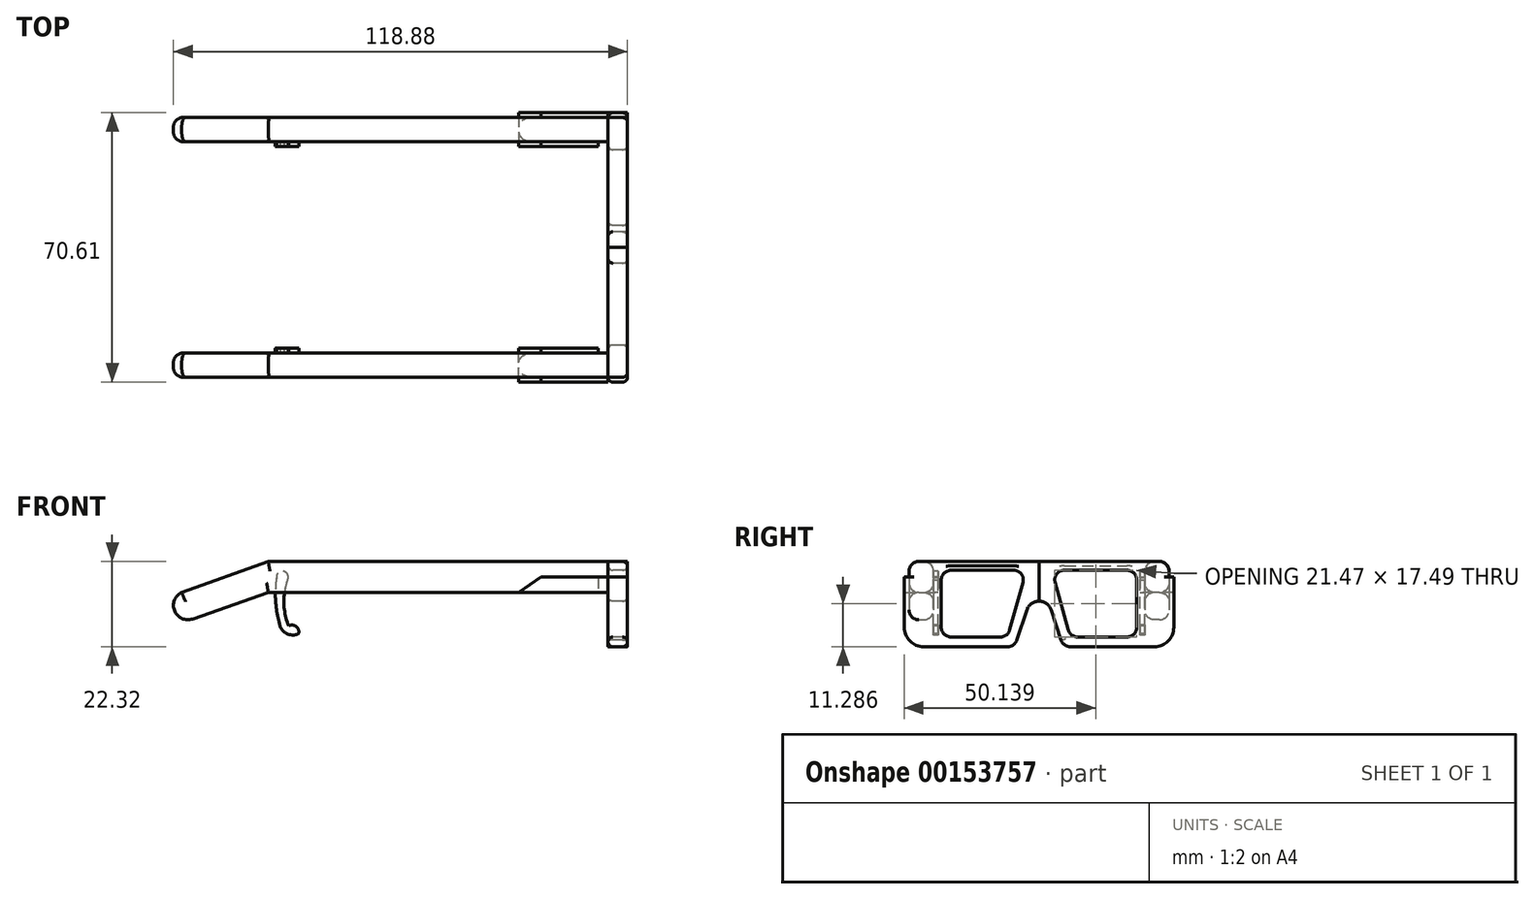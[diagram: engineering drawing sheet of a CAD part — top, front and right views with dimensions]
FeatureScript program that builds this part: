
annotation { "Feature Type Name" : "Feature", "Feature Type Description" : "" }
export const myFeature = defineFeature(function(context is Context, id is Id, definition is map)
    precondition{}
    {
        {
            var Q0;
            Q0=qCreatedBy(makeId("Front.planeOp"),FACE);
            var sketch = newSketch(context, id + "F0", { "sketchPlane" : qUnion([Q0])});
            skLineSegment(sketch, "E0", {"start": v(0, 0) * mm, "end": v(-86.43, 0) * mm});
            skLineSegment(sketch, "E1", {"start": v(0, 0) * mm, "end": v(0, -8.13) * mm});
            skLineSegment(sketch, "E2", {"start": v(0, -8.13) * mm, "end": v(-86.43, -8.13) * mm});
            skLineSegment(sketch, "E3", {"start": v(0, -4.06) * mm, "end": v(-15.06, -4.06) * mm});
            skLineSegment(sketch, "E4", {"start": v(-15.06, -4.06) * mm, "end": v(-20.83, -8.13) * mm});
            skLineSegment(sketch, "E5", {"start": v(-86.43, -8.13) * mm, "end": v(-106.28, -15.05) * mm});
            skArc(sketch, "E6", {"start": v(-106.28, -15.05) * mm, "mid": v(-110.98, -12.93) * mm, "end": v(-109.1, -8.13) * mm});
            skLineSegment(sketch, "E7", {"start": v(-86.43, 0) * mm, "end": v(-109.1, -8.13) * mm});
            skSolve(sketch);
        }
        {
            var Q0;
            {var subQ5=sQuery(id+"F0.wireOp",EDGE,"E0");Q0=makeQuery(id+"F0.imprint","IMPRINT",FACE,{"disambiguationData":[TD([[makeQuery(id+"F0.imprint","IMPRINT",EDGE,{"derivedFrom":subQ5}),1.0]])]});}
            extrude(context, id + "F1", {"entities" : qUnion([Q0]), "depth" : 6.35 * mm});
        }
        {
            var Q0;
            {var subQ3=sQuery(id+"F0.wireOp",EDGE,"E3");Q0=makeQuery(id+"F0.imprint","IMPRINT",FACE,{"disambiguationData":[TD([[makeQuery(id+"F0.imprint","IMPRINT",EDGE,{"derivedFrom":subQ3}),1.0]])]});}
            extrude(context, id + "F2", {"entities" : qUnion([Q0]), "depth" : 7.62 * mm});
        }
        {
            var Q0;
            Q0=makeQuery(id+"F1.opExtrude","CAP_EDGE",EDGE,{"disambiguationData":[OSD([sQuery(id+"F0.wireOp",EDGE,"E0")])],"isStart":false});
            var Q1;
            Q1=makeQuery(id+"F1.opExtrude","CAP_EDGE",EDGE,{"disambiguationData":[OSD([sQuery(id+"F0.wireOp",EDGE,"E0")])],"isStart":true});
            var Q2;
            Q2=makeQuery(id+"F1.opExtrude","CAP_EDGE",EDGE,{"disambiguationData":[OSD([sQuery(id+"F0.wireOp",EDGE,"E7")])],"isStart":false});
            var Q3;
            Q3=makeQuery(id+"F1.opExtrude","CAP_EDGE",EDGE,{"disambiguationData":[OSD([sQuery(id+"F0.wireOp",EDGE,"E7")])],"isStart":true});
            var Q4;
            Q4=makeQuery(id+"F1.opExtrude","CAP_EDGE",EDGE,{"disambiguationData":[OSD([sQuery(id+"F0.wireOp",EDGE,"E2")])],"isStart":false});
            var Q5;
            Q5=makeQuery(id+"F1.opExtrude","CAP_EDGE",EDGE,{"disambiguationData":[OSD([sQuery(id+"F0.wireOp",EDGE,"E5")])],"isStart":false});
            var Q6;
            Q6=makeQuery(id+"F1.opExtrude","CAP_EDGE",EDGE,{"disambiguationData":[OSD([sQuery(id+"F0.wireOp",EDGE,"E2")])],"isStart":true});
            var Q7;
            Q7=makeQuery(id+"F1.opExtrude","CAP_EDGE",EDGE,{"disambiguationData":[OSD([sQuery(id+"F0.wireOp",EDGE,"E5")])],"isStart":true});
            fillet(context, id + "F3", {"entities" : qUnion([Q0, Q1, Q2, Q3, Q4, Q5, Q6, Q7]), "radius" : 2.54 * mm, "tangentPropagation" : true, "allowEdgeOverflow" : false});
        }
        {
            var Q0;
            Q0=makeQuery(id+"F1.opExtrude","SWEPT_FACE",FACE,{"disambiguationData":[OSD([sQuery(id+"F0.wireOp",EDGE,"E1")])]});
            var Q1;
            Q1=makeQuery(id+"F2.opExtrude","SWEPT_FACE",FACE,{"disambiguationData":[OSD([sQuery(id+"F0.wireOp",EDGE,"E1")])]});
            extrude(context, id + "F4", {"entities" : qUnion([Q0, Q1]), "operationType" : NewBodyOperationType.ADD, "depth" : 2.54 * mm});
        }
        {
            var Q0;
            {var subQ3=sQuery(id+"F0.wireOp",EDGE,"E3");Q0=makeQuery(id+"F0.imprint","IMPRINT",FACE,{"disambiguationData":[TD([[makeQuery(id+"F0.imprint","IMPRINT",EDGE,{"derivedFrom":subQ3}),1.0]])]});}
            extrude(context, id + "F5", {"entities" : qUnion([Q0]), "operationType" : NewBodyOperationType.ADD, "oppositeDirection" : true, "depth" : 1.27 * mm});
        }
        {
            var Q0;
            {var subQ0=sQuery(id+"F0.wireOp",EDGE,"E1");Q0=makeQuery(id+"F4.boolean.opBoolean","MERGE",FACE,{"derivedFrom":[makeQuery(id+"F4.opExtrude","CAP_FACE",FACE,{"disambiguationData":[OSD([subQ0]),TDD([makeQuery(id+"F2.opExtrude","SWEPT_FACE",FACE,{"disambiguationData":[OSD([subQ0])]})])],"isStart":false}),makeQuery(id+"F4.opExtrude","CAP_FACE",FACE,{"disambiguationData":[OSD([subQ0]),TDD([makeQuery(id+"F1.opExtrude","SWEPT_FACE",FACE,{"disambiguationData":[OSD([subQ0])]})])],"isStart":false})]});}
            var sketch = newSketch(context, id + "F6", { "sketchPlane" : qUnion([Q0])});
            skLineSegment(sketch, "E8", {"start": v(-7.62, -8.13) * mm, "end": v(-7.62, -4.06) * mm});
            skLineSegment(sketch, "E9", {"start": v(-7.62, -4.06) * mm, "end": v(-6.35, -4.06) * mm});
            skLineSegment(sketch, "E10", {"start": v(-7.62, -8.13) * mm, "end": v(-7.62, -17.24) * mm});
            skLineSegment(sketch, "E11", {"start": v(-2.54, -22.32) * mm, "end": v(19.47, -22.32) * mm});
            skLineSegment(sketch, "E12", {"start": v(-3.81, 0) * mm, "end": v(-2.54, 0) * mm});
            skLineSegment(sketch, "E13", {"start": v(-6.35, -4.06) * mm, "end": v(-6.35, -2.54) * mm});
            skArc(sketch, "E14", {"start": v(-3.81, 0) * mm, "mid": v(-5.6, -0.74) * mm, "end": v(-6.35, -2.54) * mm});
            skPoint(sketch, "E15.visualSharp", {"position": v(-7.62, -22.32) * mm});
            skArc(sketch, "E15.filletArc", {"start": v(-7.62, -17.24) * mm, "mid": v(-6.13, -20.83) * mm, "end": v(-2.54, -22.32) * mm});
            skLineSegment(sketch, "E16", {"start": v(21.89, -20.58) * mm, "end": v(24.49, -12.69) * mm});
            skLineSegment(sketch, "E17", {"start": v(34.02, -22.32) * mm, "end": v(30.84, -12.69) * mm});
            skArc(sketch, "E18", {"start": v(30.84, -12.69) * mm, "mid": v(27.66, -10.39) * mm, "end": v(24.49, -12.69) * mm});
            skPoint(sketch, "E19.visualSharp", {"position": v(21.31, -22.32) * mm});
            skArc(sketch, "E19.filletArc", {"start": v(19.47, -22.32) * mm, "mid": v(20.96, -21.84) * mm, "end": v(21.89, -20.58) * mm});
            skLineSegment(sketch, "E20", {"start": v(-2.54, 0) * mm, "end": v(27.66, 0) * mm});
            skPoint(sketch, "E20.endSnap0", {"position": v(27.66, -10.39) * mm});
            skLineSegment(sketch, "E21", {"start": v(27.66, 0) * mm, "end": v(27.66, -10.39) * mm});
            skArc(sketch, "E22.MirrorCS", {"start": v(59.14, 0) * mm, "mid": v(60.93, -0.74) * mm, "end": v(61.68, -2.54) * mm});
            skLineSegment(sketch, "E23.MirrorCS", {"start": v(61.68, -4.06) * mm, "end": v(61.68, -2.54) * mm});
            skLineSegment(sketch, "E24.MirrorCS", {"start": v(62.95, -4.06) * mm, "end": v(61.68, -4.06) * mm});
            skLineSegment(sketch, "E25.MirrorCS", {"start": v(62.95, -8.13) * mm, "end": v(62.95, -4.06) * mm});
            skLineSegment(sketch, "E26.MirrorCS", {"start": v(62.95, -8.13) * mm, "end": v(62.95, -17.24) * mm});
            skArc(sketch, "E27.MirrorCS", {"start": v(62.95, -17.24) * mm, "mid": v(61.46, -20.83) * mm, "end": v(57.87, -22.32) * mm});
            skLineSegment(sketch, "E28.MirrorCS", {"start": v(57.87, -22.32) * mm, "end": v(35.85, -22.32) * mm});
            skLineSegment(sketch, "E29.MirrorCS", {"start": v(57.87, 0) * mm, "end": v(27.66, 0) * mm});
            skLineSegment(sketch, "E30.MirrorCS", {"start": v(59.14, 0) * mm, "end": v(57.87, 0) * mm});
            skArc(sketch, "E31.MirrorCS", {"start": v(35.85, -22.32) * mm, "mid": v(34.37, -21.84) * mm, "end": v(33.44, -20.58) * mm});
            skLineSegment(sketch, "E32", {"start": v(23.45, -5.51) * mm, "end": v(20, -17.92) * mm});
            skLineSegment(sketch, "E33", {"start": v(21, -2.29) * mm, "end": v(4.61, -2.29) * mm});
            skLineSegment(sketch, "E34", {"start": v(2.07, -4.83) * mm, "end": v(2.07, -17.24) * mm});
            skLineSegment(sketch, "E35", {"start": v(4.61, -19.78) * mm, "end": v(17.55, -19.78) * mm});
            skPoint(sketch, "E36.visualSharp", {"position": v(2.07, -19.78) * mm});
            skArc(sketch, "E36.filletArc", {"start": v(2.07, -17.24) * mm, "mid": v(2.82, -19.04) * mm, "end": v(4.61, -19.78) * mm});
            skPoint(sketch, "E37.visualSharp", {"position": v(24.35, -2.29) * mm});
            skArc(sketch, "E37.filletArc", {"start": v(23.45, -5.51) * mm, "mid": v(23.03, -3.3) * mm, "end": v(21, -2.29) * mm});
            skPoint(sketch, "E38.visualSharp", {"position": v(2.07, -2.29) * mm});
            skArc(sketch, "E38.filletArc", {"start": v(4.61, -2.29) * mm, "mid": v(2.82, -3.03) * mm, "end": v(2.07, -4.83) * mm});
            skArc(sketch, "E39.filletArc", {"start": v(17.55, -19.78) * mm, "mid": v(19.08, -19.26) * mm, "end": v(20, -17.92) * mm});
            skArc(sketch, "E40.MirrorCS", {"start": v(31.87, -5.51) * mm, "mid": v(32.3, -3.3) * mm, "end": v(34.32, -2.29) * mm});
            skLineSegment(sketch, "E41.MirrorCS", {"start": v(34.32, -2.29) * mm, "end": v(50.72, -2.29) * mm});
            skArc(sketch, "E42.MirrorCS", {"start": v(50.72, -2.29) * mm, "mid": v(52.51, -3.03) * mm, "end": v(53.26, -4.83) * mm});
            skLineSegment(sketch, "E43.MirrorCS", {"start": v(53.26, -4.83) * mm, "end": v(53.26, -17.24) * mm});
            skArc(sketch, "E44.MirrorCS", {"start": v(53.26, -17.24) * mm, "mid": v(52.51, -19.04) * mm, "end": v(50.72, -19.78) * mm});
            skLineSegment(sketch, "E45.MirrorCS", {"start": v(50.72, -19.78) * mm, "end": v(37.78, -19.78) * mm});
            skArc(sketch, "E46.MirrorCS", {"start": v(37.78, -19.78) * mm, "mid": v(36.25, -19.26) * mm, "end": v(35.34, -17.92) * mm});
            skLineSegment(sketch, "E47.MirrorCS", {"start": v(31.87, -5.51) * mm, "end": v(35.34, -17.92) * mm});
            skLineSegment(sketch, "E48", {"start": v(27.66, 0) * mm, "end": v(27.66, 9.6) * mm});
            skLineSegment(sketch, "E49", {"start": v(27.66, 9.6) * mm, "end": v(24.35, 0) * mm});
            skSolve(sketch);
        }
        {
            var Q0;
            Q0=makeQuery(id+"F6.imprint","IMPRINT",FACE,{"disambiguationData":[TD([[makeQuery(id+"F6.imprint","IMPRINT",EDGE,{"derivedFrom":sQuery(id+"F6.wireOp",EDGE,"E10")}),1.0]])]});
            var Q1;
            {var subQ0=sQuery(id+"F6.wireOp",EDGE,"E21");Q1=makeQuery(id+"F6.imprint","IMPRINT",FACE,{"disambiguationData":[TD([[makeQuery(id+"F6.imprint","IMPRINT",EDGE,{"derivedFrom":subQ0}),1.0]])]});}
            var Q2;
            Q2=makeQuery(id+"F6.imprint","IMPRINT",FACE,{"disambiguationData":[TD([[makeQuery(id+"F6.imprint","IMPRINT",EDGE,{"derivedFrom":sQuery(id+"F6.wireOp",EDGE,"E8")}),1.0]])]});
            extrude(context, id + "F7", {"entities" : qUnion([Q0, Q1, Q2]), "depth" : 5.08 * mm});
        }
        {
            var Q0;
            Q0=makeQuery(id+"F6.imprint","IMPRINT",FACE,{"disambiguationData":[TD([[makeQuery(id+"F6.imprint","IMPRINT",EDGE,{"derivedFrom":sQuery(id+"F6.wireOp",EDGE,"E32")}),-1.0]])]});
            var Q1;
            Q1=makeQuery(id+"F6.imprint","IMPRINT",FACE,{"disambiguationData":[TD([[makeQuery(id+"F6.imprint","IMPRINT",EDGE,{"derivedFrom":sQuery(id+"F6.wireOp",EDGE,"E40.MirrorCS")}),-1.0]])]});
            var Q2;
            Q2=makeQuery(id+"F7.opExtrude","CAP_FACE",FACE,{"disambiguationData":[OSD([sQuery(id+"F6.wireOp",EDGE,"E8"),sQuery(id+"F6.wireOp",EDGE,"E9"),sQuery(id+"F6.wireOp",EDGE,"E10"),sQuery(id+"F6.wireOp",EDGE,"E11"),sQuery(id+"F6.wireOp",EDGE,"E12"),sQuery(id+"F6.wireOp",EDGE,"E13"),sQuery(id+"F6.wireOp",EDGE,"E14"),sQuery(id+"F6.wireOp",EDGE,"E15.filletArc"),sQuery(id+"F6.wireOp",EDGE,"E16"),sQuery(id+"F6.wireOp",EDGE,"E17"),sQuery(id+"F6.wireOp",EDGE,"E18"),sQuery(id+"F6.wireOp",EDGE,"E19.filletArc"),sQuery(id+"F6.wireOp",EDGE,"E20"),sQuery(id+"F6.wireOp",EDGE,"E22.MirrorCS"),sQuery(id+"F6.wireOp",EDGE,"E23.MirrorCS"),sQuery(id+"F6.wireOp",EDGE,"E24.MirrorCS"),sQuery(id+"F6.wireOp",EDGE,"E25.MirrorCS"),sQuery(id+"F6.wireOp",EDGE,"E26.MirrorCS"),sQuery(id+"F6.wireOp",EDGE,"E27.MirrorCS"),sQuery(id+"F6.wireOp",EDGE,"E28.MirrorCS"),sQuery(id+"F6.wireOp",EDGE,"E29.MirrorCS"),sQuery(id+"F6.wireOp",EDGE,"E30.MirrorCS"),sQuery(id+"F6.wireOp",EDGE,"E31.MirrorCS"),sQuery(id+"F6.wireOp",EDGE,"E32"),sQuery(id+"F6.wireOp",EDGE,"E33"),sQuery(id+"F6.wireOp",EDGE,"E34"),sQuery(id+"F6.wireOp",EDGE,"E35"),sQuery(id+"F6.wireOp",EDGE,"E36.filletArc"),sQuery(id+"F6.wireOp",EDGE,"E37.filletArc"),sQuery(id+"F6.wireOp",EDGE,"E38.filletArc"),sQuery(id+"F6.wireOp",EDGE,"E39.filletArc"),sQuery(id+"F6.wireOp",EDGE,"E40.MirrorCS"),sQuery(id+"F6.wireOp",EDGE,"E41.MirrorCS"),sQuery(id+"F6.wireOp",EDGE,"E42.MirrorCS"),sQuery(id+"F6.wireOp",EDGE,"E43.MirrorCS"),sQuery(id+"F6.wireOp",EDGE,"E44.MirrorCS"),sQuery(id+"F6.wireOp",EDGE,"E45.MirrorCS"),sQuery(id+"F6.wireOp",EDGE,"E46.MirrorCS"),sQuery(id+"F6.wireOp",EDGE,"E47.MirrorCS")])],"isStart":false});
            extrude(context, id + "F8", {"entities" : qUnion([Q0, Q1]), "endBound" : BoundingType.UP_TO_SURFACE, "endBoundEntityFace" : qUnion([Q2]), "depth" : 25.4 * mm});
        }
        {
            var Q0;
            Q0=makeQuery(id+"F7.opExtrude","CAP_EDGE",EDGE,{"disambiguationData":[OSD([sQuery(id+"F6.wireOp",EDGE,"E12"),sQuery(id+"F6.wireOp",EDGE,"E20"),sQuery(id+"F6.wireOp",EDGE,"E29.MirrorCS"),sQuery(id+"F6.wireOp",EDGE,"E30.MirrorCS")])],"isStart":false});
            var Q1;
            Q1=makeQuery(id+"F7.opExtrude","CAP_EDGE",EDGE,{"disambiguationData":[OSD([sQuery(id+"F6.wireOp",EDGE,"E11")])],"isStart":false});
            var Q2;
            Q2=makeQuery(id+"F7.opExtrude","CAP_EDGE",EDGE,{"disambiguationData":[OSD([sQuery(id+"F6.wireOp",EDGE,"E28.MirrorCS")])],"isStart":false});
            var Q3;
            Q3=makeQuery(id+"F7.opExtrude","CAP_EDGE",EDGE,{"disambiguationData":[OSD([sQuery(id+"F6.wireOp",EDGE,"E41.MirrorCS")])],"isStart":false});
            var Q4;
            Q4=makeQuery(id+"F7.opExtrude","CAP_EDGE",EDGE,{"disambiguationData":[OSD([sQuery(id+"F6.wireOp",EDGE,"E43.MirrorCS")])],"isStart":true});
            var Q5;
            Q5=makeQuery(id+"F7.opExtrude","CAP_EDGE",EDGE,{"disambiguationData":[OSD([sQuery(id+"F6.wireOp",EDGE,"E33")])],"isStart":true});
            var Q6;
            Q6=makeQuery(id+"F7.opExtrude","CAP_EDGE",EDGE,{"disambiguationData":[OSD([sQuery(id+"F6.wireOp",EDGE,"E25.MirrorCS"),sQuery(id+"F6.wireOp",EDGE,"E26.MirrorCS")])],"isStart":true});
            var Q7;
            Q7=makeQuery(id+"F7.opExtrude","CAP_EDGE",EDGE,{"disambiguationData":[OSD([sQuery(id+"F6.wireOp",EDGE,"E28.MirrorCS")])],"isStart":true});
            var Q8;
            Q8=makeQuery(id+"F7.opExtrude","CAP_EDGE",EDGE,{"disambiguationData":[OSD([sQuery(id+"F6.wireOp",EDGE,"E11")])],"isStart":true});
            var Q9;
            Q9=makeQuery(id+"F7.opExtrude","CAP_EDGE",EDGE,{"disambiguationData":[OSD([sQuery(id+"F6.wireOp",EDGE,"E33")])],"isStart":false});
            fillet(context, id + "F9", {"entities" : qUnion([Q0, Q1, Q2, Q3, Q4, Q5, Q6, Q7, Q8, Q9]), "radius" : 1.27 * mm, "tangentPropagation" : true, "allowEdgeOverflow" : false});
        }
        {
            var Q0;
            Q0=makeQuery(id+"F1.opExtrude","SWEPT_BODY",BODY,{"disambiguationData":[OSD([sQuery(id+"F0.wireOp",EDGE,"E0"),sQuery(id+"F0.wireOp",EDGE,"E1"),sQuery(id+"F0.wireOp",EDGE,"E2"),sQuery(id+"F0.wireOp",EDGE,"E3"),sQuery(id+"F0.wireOp",EDGE,"E4"),sQuery(id+"F0.wireOp",EDGE,"E5"),sQuery(id+"F0.wireOp",EDGE,"E6"),sQuery(id+"F0.wireOp",EDGE,"E7")])]});
            var Q1;
            Q1=makeQuery(id+"F2.opExtrude","SWEPT_BODY",BODY,{"disambiguationData":[OSD([sQuery(id+"F0.wireOp",EDGE,"E1"),sQuery(id+"F0.wireOp",EDGE,"E2"),sQuery(id+"F0.wireOp",EDGE,"E3"),sQuery(id+"F0.wireOp",EDGE,"E4")])]});
            var Q2;
            Q2=qCreatedBy(makeId("Front.planeOp"),FACE);
            mirror(context, id + "F10", {"entities" : qUnion([Q0, Q1]), "mirrorPlane" : qUnion([Q2])});
        }
        {
            var Q0;
            Q0=makeQuery(id+"F10.opPattern","COPY",BODY,{"derivedFrom":makeQuery(id+"F2.opExtrude","SWEPT_BODY",BODY,{"disambiguationData":[OSD([sQuery(id+"F0.wireOp",EDGE,"E1"),sQuery(id+"F0.wireOp",EDGE,"E2"),sQuery(id+"F0.wireOp",EDGE,"E3"),sQuery(id+"F0.wireOp",EDGE,"E4")])]}),"instanceName":"1"});
            var Q1;
            Q1=makeQuery(id+"F10.opPattern","COPY",BODY,{"derivedFrom":makeQuery(id+"F1.opExtrude","SWEPT_BODY",BODY,{"disambiguationData":[OSD([sQuery(id+"F0.wireOp",EDGE,"E0"),sQuery(id+"F0.wireOp",EDGE,"E1"),sQuery(id+"F0.wireOp",EDGE,"E2"),sQuery(id+"F0.wireOp",EDGE,"E3"),sQuery(id+"F0.wireOp",EDGE,"E4"),sQuery(id+"F0.wireOp",EDGE,"E5"),sQuery(id+"F0.wireOp",EDGE,"E6"),sQuery(id+"F0.wireOp",EDGE,"E7")])]}),"instanceName":"1"});
            var Q2;
            {var subQ0=sQuery(id+"F6.wireOp",EDGE,"E30.MirrorCS");var subQ1=sQuery(id+"F6.wireOp",EDGE,"E29.MirrorCS");var subQ2=sQuery(id+"F6.wireOp",EDGE,"E20");var subQ3=sQuery(id+"F6.wireOp",EDGE,"E12");Q2=makeQuery(id+"F9.opFillet","BLEND_EDGE",EDGE,{"blendedFrom":[makeQuery(id+"F7.opExtrude","CAP_EDGE",EDGE,{"disambiguationData":[OSD([subQ3,subQ2,subQ1,subQ0])],"isStart":false}),makeQuery(id+"F7.opExtrude","SWEPT_FACE",FACE,{"disambiguationData":[OSD([subQ3,subQ2,subQ1,subQ0])]})],"blendedInto":[makeQuery(id+"F7.opExtrude","SWEPT_FACE",FACE,{"disambiguationData":[OSD([subQ3,subQ2,subQ1,subQ0])]})]});}
            transform(context, id + "F11", {"entities" : qUnion([Q0, Q1]), "transformType" : TransformType.TRANSLATION_DISTANCE, "transformDirection" : qUnion([Q2]), "distance" : 55.37 * mm, "makeCopy" : false});
        }
        {
            var Q0;
            Q0=makeQuery(id+"F1.opExtrude","CAP_FACE",FACE,{"disambiguationData":[OSD([sQuery(id+"F0.wireOp",EDGE,"E0"),sQuery(id+"F0.wireOp",EDGE,"E1"),sQuery(id+"F0.wireOp",EDGE,"E2"),sQuery(id+"F0.wireOp",EDGE,"E3"),sQuery(id+"F0.wireOp",EDGE,"E4"),sQuery(id+"F0.wireOp",EDGE,"E5"),sQuery(id+"F0.wireOp",EDGE,"E6"),sQuery(id+"F0.wireOp",EDGE,"E7")])],"isStart":true});
            var sketch = newSketch(context, id + "F12", { "sketchPlane" : qUnion([Q0])});
            skCircle(sketch, "E50", {"center": v(82.74, -4.1) * mm, "radius": 1.55 * mm});
            skArc(sketch, "E51", {"start": v(81.1, -16.87) * mm, "mid": v(82.36, -10.61) * mm, "end": v(81.2, -4.34) * mm});
            skArc(sketch, "E52", {"start": v(83.36, -16.87) * mm, "mid": v(84.5, -10.6) * mm, "end": v(84.29, -4.24) * mm});
            skArc(sketch, "E53", {"start": v(78.5, -18.95) * mm, "mid": v(81.39, -18.98) * mm, "end": v(83.36, -16.87) * mm});
            skArc(sketch, "E54", {"start": v(81.1, -16.87) * mm, "mid": v(79.11, -17.06) * mm, "end": v(78.5, -18.95) * mm});
            skSolve(sketch);
        }
        {
            var Q0;
            Q0 = qSketchRegion(id + "F12", true);
            extrude(context, id + "F13", {"entities" : qUnion([Q0]), "depth" : 1.27 * mm});
        }
        {
            var Q0;
            Q0=makeQuery(id+"F13.opExtrude","SWEPT_BODY",BODY,{"disambiguationData":[OSD([sQuery(id+"F12.wireOp",EDGE,"E50"),sQuery(id+"F12.wireOp",EDGE,"E51"),sQuery(id+"F12.wireOp",EDGE,"E52"),sQuery(id+"F12.wireOp",EDGE,"E53"),sQuery(id+"F12.wireOp",EDGE,"E54")])]});
            var Q1;
            Q1=makeQuery(id+"F7.opExtrude","CAP_EDGE",EDGE,{"disambiguationData":[OSD([sQuery(id+"F6.wireOp",EDGE,"E12"),sQuery(id+"F6.wireOp",EDGE,"E20"),sQuery(id+"F6.wireOp",EDGE,"E29.MirrorCS"),sQuery(id+"F6.wireOp",EDGE,"E30.MirrorCS")])],"isStart":true});
            transform(context, id + "F14", {"entities" : qUnion([Q0]), "transformType" : TransformType.TRANSLATION_DISTANCE, "transformDirection" : qUnion([Q1]), "distance" : 38.1 * mm, "makeCopy" : true});
        }
        {
            var Q0;
            Q0=makeQuery(id+"F14.opPattern","COPY",BODY,{"derivedFrom":makeQuery(id+"F13.opExtrude","SWEPT_BODY",BODY,{"disambiguationData":[OSD([sQuery(id+"F12.wireOp",EDGE,"E50"),sQuery(id+"F12.wireOp",EDGE,"E51"),sQuery(id+"F12.wireOp",EDGE,"E52"),sQuery(id+"F12.wireOp",EDGE,"E53"),sQuery(id+"F12.wireOp",EDGE,"E54")])]}),"instanceName":"1"});
            var Q1;
            Q1=makeQuery(id+"F7.opExtrude","CAP_EDGE",EDGE,{"disambiguationData":[OSD([sQuery(id+"F6.wireOp",EDGE,"E12"),sQuery(id+"F6.wireOp",EDGE,"E20"),sQuery(id+"F6.wireOp",EDGE,"E29.MirrorCS"),sQuery(id+"F6.wireOp",EDGE,"E30.MirrorCS")])],"isStart":true});
            transform(context, id + "F15", {"entities" : qUnion([Q0]), "transformType" : TransformType.TRANSLATION_DISTANCE, "transformDirection" : qUnion([Q1]), "distance" : 16 * mm, "makeCopy" : false});
        }
    });
